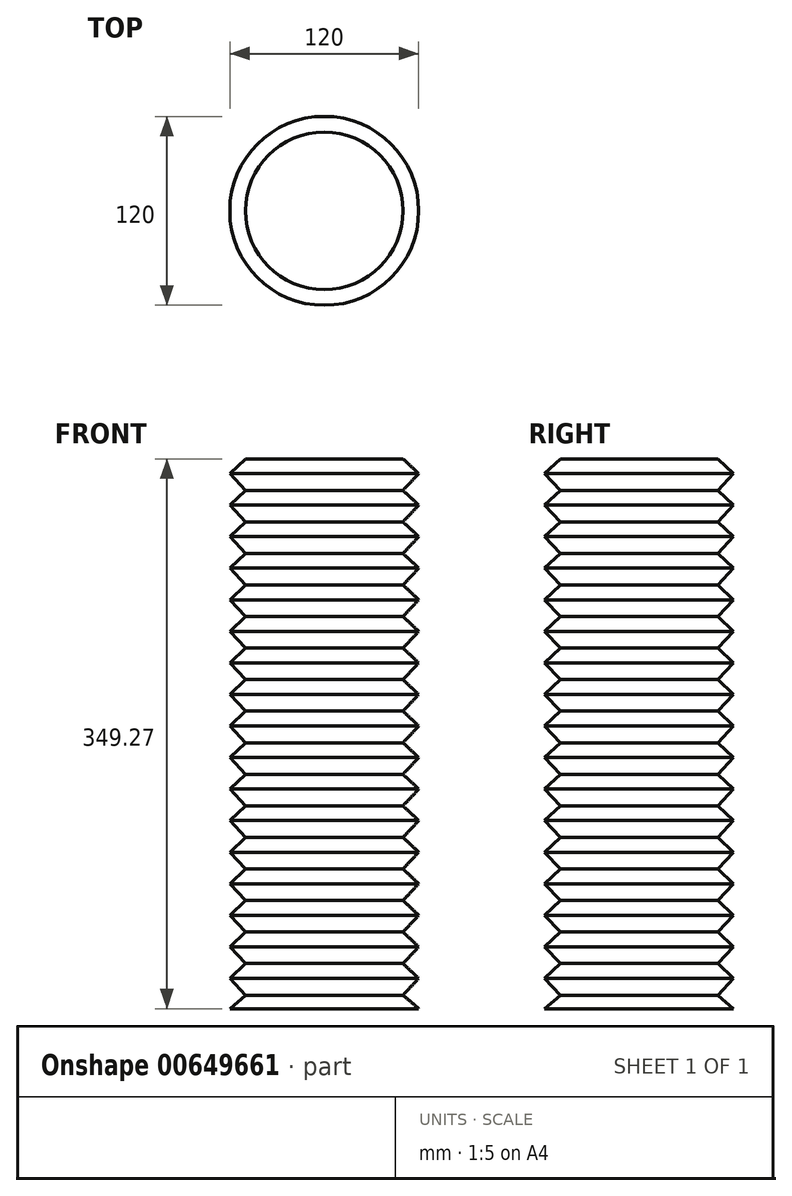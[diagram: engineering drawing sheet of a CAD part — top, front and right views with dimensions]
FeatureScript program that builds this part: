
annotation { "Feature Type Name" : "Feature", "Feature Type Description" : "" }
export const myFeature = defineFeature(function(context is Context, id is Id, definition is map)
    precondition{}
    {
        {
            var Q0;
            Q0=qCreatedBy(makeId("Front.planeOp"),FACE);
            var sketch = newSketch(context, id + "F0", { "sketchPlane" : qUnion([Q0])});
            skLineSegment(sketch, "E0", {"start": v(-42.1, 157.7) * mm, "end": v(-52.1, 148.3) * mm});
            skLineSegment(sketch, "E1", {"start": v(-52.1, 148.3) * mm, "end": v(-42.1, 137.65) * mm});
            skLineSegment(sketch, "E2", {"start": v(-42.1, 137.65) * mm, "end": v(-52.1, 128.26) * mm});
            skLineSegment(sketch, "E3", {"start": v(-52.1, 128.26) * mm, "end": v(-42.1, 117.61) * mm});
            skLineSegment(sketch, "E4", {"start": v(-42.1, 117.61) * mm, "end": v(-52.1, 108.22) * mm});
            skLineSegment(sketch, "E5", {"start": v(-52.1, 108.22) * mm, "end": v(-42.1, 97.57) * mm});
            skLineSegment(sketch, "E6", {"start": v(-42.1, 97.57) * mm, "end": v(-52.1, 88.18) * mm});
            skLineSegment(sketch, "E7", {"start": v(-52.1, 88.18) * mm, "end": v(-42.1, 77.53) * mm});
            skLineSegment(sketch, "E8", {"start": v(-42.1, 77.53) * mm, "end": v(-52.1, 68.14) * mm});
            skLineSegment(sketch, "E9", {"start": v(-52.1, 68.14) * mm, "end": v(-42.1, 57.5) * mm});
            skLineSegment(sketch, "E10", {"start": v(-42.1, 57.5) * mm, "end": v(-52.1, 48.1) * mm});
            skLineSegment(sketch, "E11", {"start": v(-52.1, 48.1) * mm, "end": v(-42.1, 37.45) * mm});
            skLineSegment(sketch, "E12", {"start": v(-42.1, 37.45) * mm, "end": v(-52.1, 28.06) * mm});
            skLineSegment(sketch, "E13", {"start": v(-52.1, 28.06) * mm, "end": v(-42.1, 17.41) * mm});
            skLineSegment(sketch, "E14", {"start": v(-42.1, 17.41) * mm, "end": v(-52.1, 8.02) * mm});
            skLineSegment(sketch, "E15", {"start": v(-52.1, 8.02) * mm, "end": v(-42.1, -2.63) * mm});
            skLineSegment(sketch, "E16", {"start": v(-42.1, -2.63) * mm, "end": v(-52.1, -12.02) * mm});
            skLineSegment(sketch, "E17", {"start": v(-52.1, -12.02) * mm, "end": v(-42.1, -22.67) * mm});
            skLineSegment(sketch, "E18", {"start": v(-42.1, -22.67) * mm, "end": v(-52.1, -32.06) * mm});
            skLineSegment(sketch, "E19", {"start": v(-52.1, -32.06) * mm, "end": v(-42.1, -42.7) * mm});
            skLineSegment(sketch, "E20", {"start": v(-42.1, -42.7) * mm, "end": v(-52.1, -52.1) * mm});
            skLineSegment(sketch, "E21", {"start": v(-52.1, -52.1) * mm, "end": v(-42.1, -62.75) * mm});
            skLineSegment(sketch, "E22", {"start": v(-42.1, -62.75) * mm, "end": v(-52.1, -72.14) * mm});
            skLineSegment(sketch, "E23", {"start": v(-52.1, -72.14) * mm, "end": v(-42.1, -82.79) * mm});
            skLineSegment(sketch, "E24", {"start": v(-42.1, -82.79) * mm, "end": v(-52.1, -92.17) * mm});
            skLineSegment(sketch, "E25", {"start": v(-52.1, -92.17) * mm, "end": v(-42.1, -102.83) * mm});
            skLineSegment(sketch, "E26", {"start": v(-42.1, -102.83) * mm, "end": v(-52.1, -112.21) * mm});
            skLineSegment(sketch, "E27", {"start": v(-52.1, -112.21) * mm, "end": v(-42.1, -122.86) * mm});
            skLineSegment(sketch, "E28", {"start": v(-42.1, -122.86) * mm, "end": v(-52.1, -132.25) * mm});
            skLineSegment(sketch, "E29", {"start": v(-52.1, -132.25) * mm, "end": v(-42.1, -142.9) * mm});
            skLineSegment(sketch, "E30", {"start": v(-42.1, -142.9) * mm, "end": v(-52.1, -152.3) * mm});
            skLineSegment(sketch, "E31", {"start": v(-52.1, -152.3) * mm, "end": v(-42.1, -162.94) * mm});
            skLineSegment(sketch, "E32", {"start": v(-42.1, -162.94) * mm, "end": v(-52.1, -172.33) * mm});
            skLineSegment(sketch, "E33", {"start": v(-52.1, -172.33) * mm, "end": v(-42.1, -182.98) * mm});
            skLineSegment(sketch, "E34", {"start": v(-42.1, -182.98) * mm, "end": v(-52.1, -191.58) * mm});
            skLineSegment(sketch, "E35", {"start": v(-52.1, -191.58) * mm, "end": v(7.9, -191.58) * mm});
            skLineSegment(sketch, "E36", {"start": v(7.9, 157.7) * mm, "end": v(7.9, -191.58) * mm});
            skLineSegment(sketch, "E37", {"start": v(-42.1, 157.7) * mm, "end": v(7.9, 157.7) * mm});
            skSolve(sketch);
        }
        {
            var Q0;
            Q0 = qSketchRegion(id + "F0", true);
            var Q1;
            Q1=sQuery(id+"F0.wireOp",EDGE,"E36");
            revolve(context, id + "F1", {"entities" : qUnion([Q0]), "axis" : qUnion([Q1]), "revolveType" : RevolveType.FULL});
        }
    });
